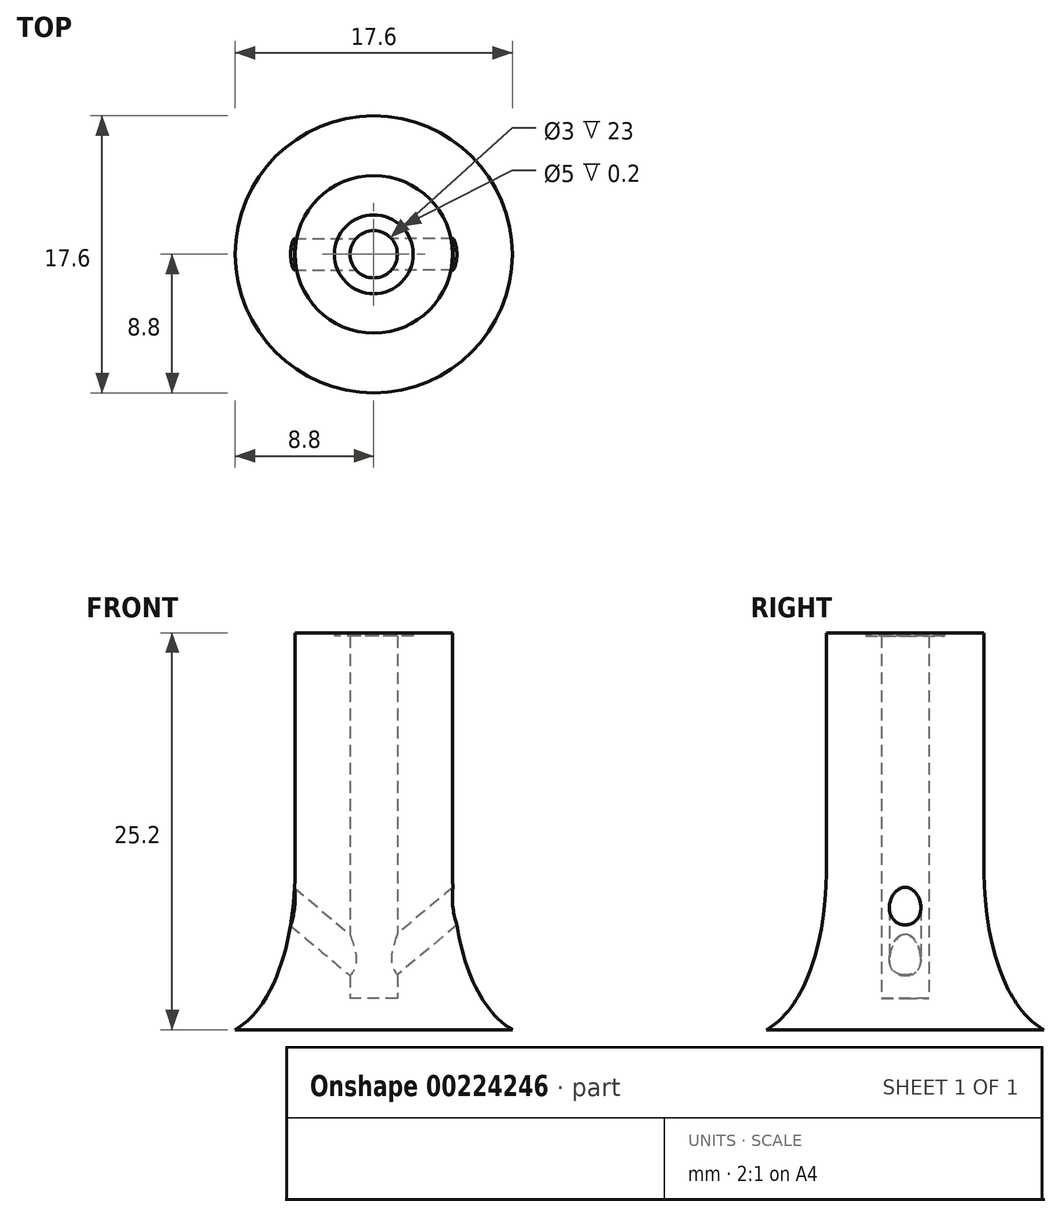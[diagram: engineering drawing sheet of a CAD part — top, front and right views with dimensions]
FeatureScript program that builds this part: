
annotation { "Feature Type Name" : "Feature", "Feature Type Description" : "" }
export const myFeature = defineFeature(function(context is Context, id is Id, definition is map)
    precondition{}
    {
        {
            var Q0;
            Q0=qCreatedBy(makeId("Top.planeOp"),FACE);
            var sketch = newSketch(context, id + "F0", { "sketchPlane" : qUnion([Q0])});
            skCircle(sketch, "E0", {"center": v(0, 0) * mm, "radius": 2.5 * mm});
            skCircle(sketch, "E1", {"center": v(0, 0) * mm, "radius": 1.5 * mm});
            skSolve(sketch);
        }
        {
            var Q0;
            Q0=qCreatedBy(makeId("Front.planeOp"),FACE);
            var sketch = newSketch(context, id + "F1", { "sketchPlane" : qUnion([Q0])});
            skLineSegment(sketch, "E2", {"start": v(0, -11.16) * mm, "end": v(0, 13.12) * mm, "construction": true});
            skLineSegment(sketch, "E3", {"start": v(0, -6.47) * mm, "end": v(7.66, -0.05) * mm});
            skLineSegment(sketch, "E4.MirrorCS", {"start": v(0, -6.47) * mm, "end": v(-7.66, -0.05) * mm});
            skSolve(sketch);
        }
        {
            var Q0;
            Q0=sQuery(id+"F1.wireOp",EDGE,"E3");
            var Q1;
            Q1=sQuery(id+"F1.wireOp",VERTEX,"E3.end");
            cPlane(context, id + "F2", {"entities" : qUnion([Q0, Q1]), "cplaneType" : CPlaneType.CURVE_POINT, "offset" : 25 * mm, "width" : 150 * mm, "height" : 150 * mm});
        }
        {
            var Q0;
            Q0=qCreatedBy(id+"F2.planeOp",FACE);
            var sketch = newSketch(context, id + "F3", { "sketchPlane" : qUnion([Q0])});
            skLineSegment(sketch, "E5.0", {"start": v(0, -8.55) * mm, "end": v(0, 10.05) * mm, "construction": true});
            skLineSegment(sketch, "E6", {"start": v(0, 0) * mm, "end": v(9.07, 0) * mm, "construction": true});
            skCircle(sketch, "E7", {"center": v(0, -4.96) * mm, "radius": 1 * mm});
            skSolve(sketch);
        }
        {
            var Q0;
            Q0=makeQuery(id+"F0.imprint","IMPRINT",FACE,{"disambiguationData":[TD([[makeQuery(id+"F0.imprint","IMPRINT",EDGE,{"derivedFrom":sQuery(id+"F0.wireOp",EDGE,"E0")}),1.0]])]});
            extrude(context, id + "F4", {"entities" : qUnion([Q0]), "depth" : 15 * mm, "hasSecondDirection" : true, "secondDirectionOppositeDirection" : true, "secondDirectionDepth" : 10 * mm});
        }
        {
            var Q0;
            Q0=makeQuery(id+"F4.opExtrude","CAP_FACE",FACE,{"disambiguationData":[OSD([sQuery(id+"F0.wireOp",EDGE,"E0"),sQuery(id+"F0.wireOp",EDGE,"E1")])],"isStart":false});
            cPlane(context, id + "F5", {"entities" : qUnion([Q0]), "cplaneType" : CPlaneType.OFFSET, "offset" : 5 * mm, "width" : 150 * mm, "height" : 150 * mm});
        }
        {
            var Q0;
            Q0=makeQuery(id+"F4.opExtrude","CAP_FACE",FACE,{"disambiguationData":[OSD([sQuery(id+"F0.wireOp",EDGE,"E0"),sQuery(id+"F0.wireOp",EDGE,"E1")])],"isStart":false});
            var sketch = newSketch(context, id + "F6", { "sketchPlane" : qUnion([Q0])});
            skCircle(sketch, "E8.0", {"center": v(0, 0) * mm, "radius": 1.5 * mm});
            skCircle(sketch, "E9", {"center": v(0, 0) * mm, "radius": 2.55 * mm});
            skSolve(sketch);
        }
        {
            var Q0;
            Q0=makeQuery(id+"F6.imprint","IMPRINT",FACE,{"disambiguationData":[TD([[makeQuery(id+"F6.imprint","IMPRINT",EDGE,{"derivedFrom":sQuery(id+"F6.wireOp",EDGE,"E9")}),1.0]])]});
            extrude(context, id + "F7", {"entities" : qUnion([Q0]), "operationType" : NewBodyOperationType.ADD, "oppositeDirection" : true, "depth" : .25 * mm});
        }
        {
            var Q0;
            Q0=qCreatedBy(id+"F5.planeOp",FACE);
            var sketch = newSketch(context, id + "F8", { "sketchPlane" : qUnion([Q0])});
            skCircle(sketch, "E10", {"center": v(0, 0) * mm, "radius": 2 * mm});
            skCircle(sketch, "E11", {"center": v(0, 0) * mm, "radius": 1.5 * mm});
            skSolve(sketch);
        }
        {
            var Q0;
            Q0=qCreatedBy(makeId("Front.planeOp"),FACE);
            var sketch = newSketch(context, id + "F9", { "sketchPlane" : qUnion([Q0])});
            skLineSegment(sketch, "E12.0", {"start": v(-2, 20) * mm, "end": v(2, 20) * mm});
            skLineSegment(sketch, "E13.0", {"start": v(-1.5, 20) * mm, "end": v(1.5, 20) * mm});
            skLineSegment(sketch, "E14.0", {"start": v(-2.55, 15) * mm, "end": v(2.55, 15) * mm});
            skLineSegment(sketch, "E15.0", {"start": v(-1.5, 15) * mm, "end": v(1.5, 15) * mm});
            skFitSpline(sketch, "E16", {"points": [v(-2.55, 15) * mm, v(-2, 20) * mm], "startDerivative": vector(0.55, 5) * mm, "endDerivative": vector(0.08, 5.34) * mm});
            skLineSegment(sketch, "E17", {"start": v(-1.5, 15) * mm, "end": v(-1.5, 20) * mm});
            skLineSegment(sketch, "E18", {"start": v(0, 0.37) * mm, "end": v(0, 14.35) * mm, "construction": true});
            skPoint(sketch, "E18.endSnap0", {"position": v(0, 20) * mm});
            skSolve(sketch);
        }
        {
            var Q0;
            Q0=qCreatedBy(makeId("Top.planeOp"),FACE);
            var sketch = newSketch(context, id + "F10", { "sketchPlane" : qUnion([Q0])});
            skCircle(sketch, "E19", {"center": v(0, 0) * mm, "radius": 5 * mm});
            skCircle(sketch, "E20.0", {"center": v(0, 0) * mm, "radius": 1.5 * mm});
            skSolve(sketch);
        }
        {
            var Q0;
            Q0=makeQuery(id+"F10.imprint","IMPRINT",FACE,{"disambiguationData":[TD([[makeQuery(id+"F10.imprint","IMPRINT",EDGE,{"derivedFrom":sQuery(id+"F10.wireOp",EDGE,"E19")}),1.0]])]});
            extrude(context, id + "F11", {"entities" : qUnion([Q0]), "operationType" : NewBodyOperationType.ADD, "depth" : 1.2 * mm});
        }
        {
            var Q0;
            Q0=qCreatedBy(makeId("Front.planeOp"),FACE);
            var sketch = newSketch(context, id + "F12", { "sketchPlane" : qUnion([Q0])});
            skLineSegment(sketch, "E21.0", {"start": v(-2.5, -10) * mm, "end": v(2.5, -10) * mm});
            skLineSegment(sketch, "E22.0", {"start": v(-5, 0) * mm, "end": v(5, 0) * mm});
            skLineSegment(sketch, "E23", {"start": v(2.5, -10) * mm, "end": v(8.8, -10) * mm});
            skFitSpline(sketch, "E24", {"points": [v(5, 0) * mm, v(8.8, -10) * mm], "startDerivative": vector(0.12, -13.45) * mm, "endDerivative": vector(7.4, -4.28) * mm});
            skLineSegment(sketch, "E25", {"start": v(2.5, -10) * mm, "end": v(2.5, 0) * mm});
            skLineSegment(sketch, "E26", {"start": v(0, 0) * mm, "end": v(0, -15.25) * mm, "construction": true});
            skSolve(sketch);
        }
        {
            var Q0;
            Q0=makeQuery(id+"F12.imprint","IMPRINT",FACE,{"disambiguationData":[TD([[makeQuery(id+"F12.imprint","IMPRINT",EDGE,{"derivedFrom":sQuery(id+"F12.wireOp",EDGE,"E23")}),1.0]])]});
            var Q1;
            Q1=sQuery(id+"F12.wireOp",EDGE,"E26");
            revolve(context, id + "F13", {"operationType" : NewBodyOperationType.ADD, "entities" : qUnion([Q0]), "axis" : qUnion([Q1]), "revolveType" : RevolveType.FULL});
        }
        {
            var Q0;
            Q0=makeQuery(id+"F13.boolean.opBoolean","MERGE",FACE,{"derivedFrom":[makeQuery(id+"F4.opExtrude","CAP_FACE",FACE,{"disambiguationData":[OSD([sQuery(id+"F0.wireOp",EDGE,"E0"),sQuery(id+"F0.wireOp",EDGE,"E1")])],"isStart":true}),makeQuery(id+"F13.opRevolve","SWEPT_FACE",FACE,{"disambiguationData":[OSD([sQuery(id+"F12.wireOp",EDGE,"E23")])]})]});
            var sketch = newSketch(context, id + "F14", { "sketchPlane" : qUnion([Q0])});
            skCircle(sketch, "E27.0", {"center": v(0, 0) * mm, "radius": 1.5 * mm});
            skSolve(sketch);
        }
        {
            var Q0;
            Q0=makeQuery(id+"F14.imprint","IMPRINT",FACE,{"disambiguationData":[TD([[makeQuery(id+"F14.imprint","IMPRINT",EDGE,{"derivedFrom":sQuery(id+"F14.wireOp",EDGE,"E27.0")}),-1.0]])]});
            extrude(context, id + "F15", {"entities" : qUnion([Q0]), "operationType" : NewBodyOperationType.ADD, "oppositeDirection" : true, "depth" : 2 * mm});
        }
        {
            var Q0;
            Q0=makeQuery(id+"F3.imprint","IMPRINT",FACE,{"disambiguationData":[TD([[makeQuery(id+"F3.imprint","IMPRINT",EDGE,{"derivedFrom":sQuery(id+"F3.wireOp",EDGE,"E7")}),1.0]])]});
            var Q1;
            Q1=sQuery(id+"F1.wireOp",EDGE,"E3");
            sweep(context, id + "F16", {"operationType" : NewBodyOperationType.REMOVE, "profiles" : qUnion([Q0]), "path" : qUnion([Q1])});
        }
        {
            var Q0;
            Q0=sQuery(id+"F1.wireOp",VERTEX,"E4.MirrorCS.end");
            var Q1;
            Q1=sQuery(id+"F1.wireOp",EDGE,"E4.MirrorCS");
            cPlane(context, id + "F17", {"entities" : qUnion([Q0, Q1]), "cplaneType" : CPlaneType.LINE_POINT, "offset" : 25 * mm, "width" : 150 * mm, "height" : 150 * mm});
        }
        {
            var Q0;
            Q0=qCreatedBy(id+"F17.planeOp",FACE);
            var sketch = newSketch(context, id + "F18", { "sketchPlane" : qUnion([Q0])});
            skCircle(sketch, "E28", {"center": v(0, -5) * mm, "radius": 1 * mm});
            skSolve(sketch);
        }
        {
            var Q0;
            Q0=makeQuery(id+"F18.imprint","IMPRINT",FACE,{"disambiguationData":[TD([[makeQuery(id+"F18.imprint","IMPRINT",EDGE,{"derivedFrom":sQuery(id+"F18.wireOp",EDGE,"E28")}),1.0]])]});
            var Q1;
            Q1=sQuery(id+"F1.wireOp",EDGE,"E4.MirrorCS");
            sweep(context, id + "F19", {"operationType" : NewBodyOperationType.REMOVE, "profiles" : qUnion([Q0]), "path" : qUnion([Q1])});
        }
        {
            var Q0;
            Q0=makeQuery(id+"F11.opExtrude","CAP_FACE",FACE,{"disambiguationData":[OSD([sQuery(id+"F10.wireOp",EDGE,"E19"),sQuery(id+"F10.wireOp",EDGE,"E20.0")])],"isStart":false});
            extrude(context, id + "F20", {"entities" : qUnion([Q0]), "operationType" : NewBodyOperationType.ADD, "depth" : 14 * mm});
        }
    });
